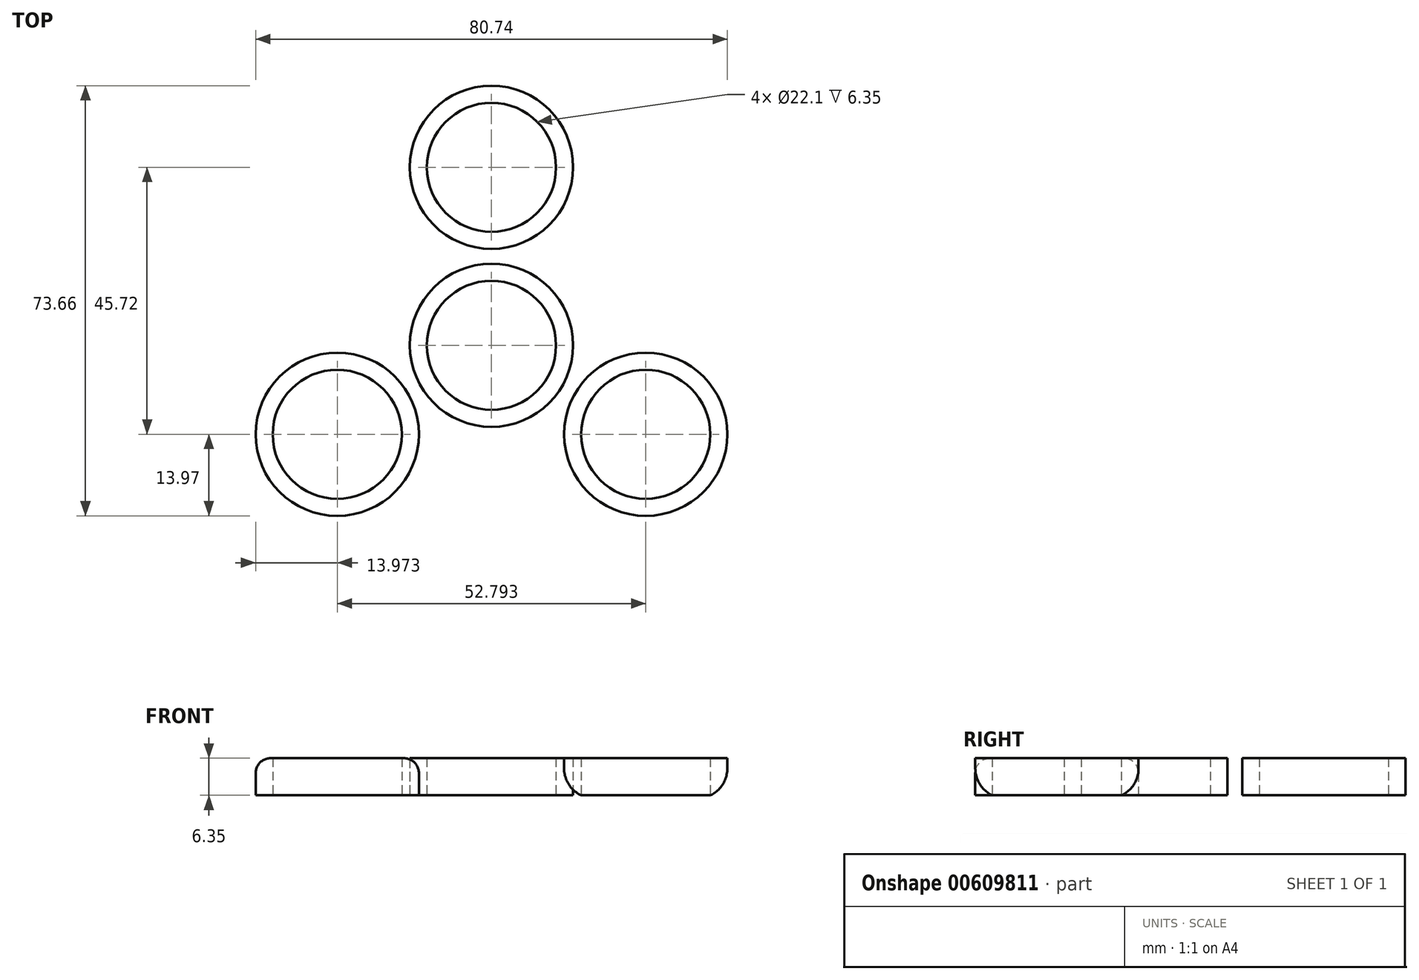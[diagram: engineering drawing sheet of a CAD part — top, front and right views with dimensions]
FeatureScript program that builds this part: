
annotation { "Feature Type Name" : "Feature", "Feature Type Description" : "" }
export const myFeature = defineFeature(function(context is Context, id is Id, definition is map)
    precondition{}
    {
        {
            var Q0;
            Q0=qCreatedBy(makeId("Top.planeOp"),FACE);
            var sketch = newSketch(context, id + "F0", { "sketchPlane" : qUnion([Q0])});
            skCircle(sketch, "E0", {"center": v(0, 0) * mm, "radius": 11.05 * mm});
            skCircle(sketch, "E1", {"center": v(0, 0) * mm, "radius": 13.97 * mm});
            skCircle(sketch, "E2", {"center": v(0, 30.48) * mm, "radius": 11.05 * mm});
            skCircle(sketch, "E3", {"center": v(0, 30.48) * mm, "radius": 13.97 * mm});
            skCircle(sketch, "E4.1.0", {"center": v(-26.4, -15.24) * mm, "radius": 13.97 * mm});
            skCircle(sketch, "E4.1.1", {"center": v(-26.4, -15.24) * mm, "radius": 11.05 * mm});
            skCircle(sketch, "E4.2.0", {"center": v(26.4, -15.24) * mm, "radius": 13.97 * mm});
            skCircle(sketch, "E4.2.1", {"center": v(26.4, -15.24) * mm, "radius": 11.05 * mm});
            skSolve(sketch);
        }
        {
            var Q0;
            Q0=qCreatedBy(makeId("Top.planeOp"),FACE);
            var sketch = newSketch(context, id + "F1", { "sketchPlane" : qUnion([Q0])});
            skSolve(sketch);
        }
        {
            var Q0;
            Q0 = qSketchRegion(id + "F1", true);
            var Q1;
            Q1=makeQuery(id+"F0.imprint","IMPRINT",FACE,{"disambiguationData":[TD([[makeQuery(id+"F0.imprint","IMPRINT",EDGE,{"derivedFrom":sQuery(id+"F0.wireOp",EDGE,"E2")}),-1.0]])]});
            var Q2;
            Q2=makeQuery(id+"F0.imprint","IMPRINT",FACE,{"disambiguationData":[TD([[makeQuery(id+"F0.imprint","IMPRINT",EDGE,{"derivedFrom":sQuery(id+"F0.wireOp",EDGE,"E0")}),-1.0]])]});
            var Q3;
            Q3=makeQuery(id+"F0.imprint","IMPRINT",FACE,{"disambiguationData":[TD([[makeQuery(id+"F0.imprint","IMPRINT",EDGE,{"derivedFrom":sQuery(id+"F0.wireOp",EDGE,"E4.2.0")}),1.0]])]});
            var Q4;
            Q4=makeQuery(id+"F0.imprint","IMPRINT",FACE,{"disambiguationData":[TD([[makeQuery(id+"F0.imprint","IMPRINT",EDGE,{"derivedFrom":sQuery(id+"F0.wireOp",EDGE,"E4.1.0")}),1.0]])]});
            extrude(context, id + "F2", {"entities" : qUnion([Q0, Q1, Q2, Q3, Q4]), "depth" : 6.35 * mm, "offsetDistance" : 25.4 * mm});
        }
        {
            var Q0;
            Q0=makeQuery(id+"F2.opExtrude","CAP_EDGE",EDGE,{"disambiguationData":[OSD([sQuery(id+"F0.wireOp",EDGE,"E4.1.0")])],"isStart":false});
            var Q1;
            Q1=makeQuery(id+"F2.opExtrude","CAP_EDGE",EDGE,{"disambiguationData":[OSD([sQuery(id+"F0.wireOp",EDGE,"E4.1.0")])],"isStart":true});
            var Q2;
            Q2=makeQuery(id+"F2.opExtrude","CAP_EDGE",EDGE,{"disambiguationData":[OSD([sQuery(id+"F0.wireOp",EDGE,"E4.2.0")])],"isStart":true});
            var Q3;
            Q3=makeQuery(id+"F2.opExtrude","CAP_EDGE",EDGE,{"disambiguationData":[OSD([sQuery(id+"F0.wireOp",EDGE,"E3")])],"isStart":false});
            var Q4;
            Q4=makeQuery(id+"F2.opExtrude","CAP_EDGE",EDGE,{"disambiguationData":[OSD([sQuery(id+"F0.wireOp",EDGE,"E3")])],"isStart":true});
            fillet(context, id + "F3", {"entities" : qUnion([Q0, Q1, Q2, Q3, Q4]), "radius" : 5.08 * mm, "tangentPropagation" : true, "allowEdgeOverflow" : false});
        }
        {
            var Q0;
            Q0=makeQuery(id+"F2.opExtrude","CAP_EDGE",EDGE,{"disambiguationData":[OSD([sQuery(id+"F0.wireOp",EDGE,"E4.1.0")])],"isStart":false});
            fillet(context, id + "F4", {"entities" : qUnion([Q0]), "radius" : 2.54 * mm, "tangentPropagation" : true, "allowEdgeOverflow" : false});
        }
    });
